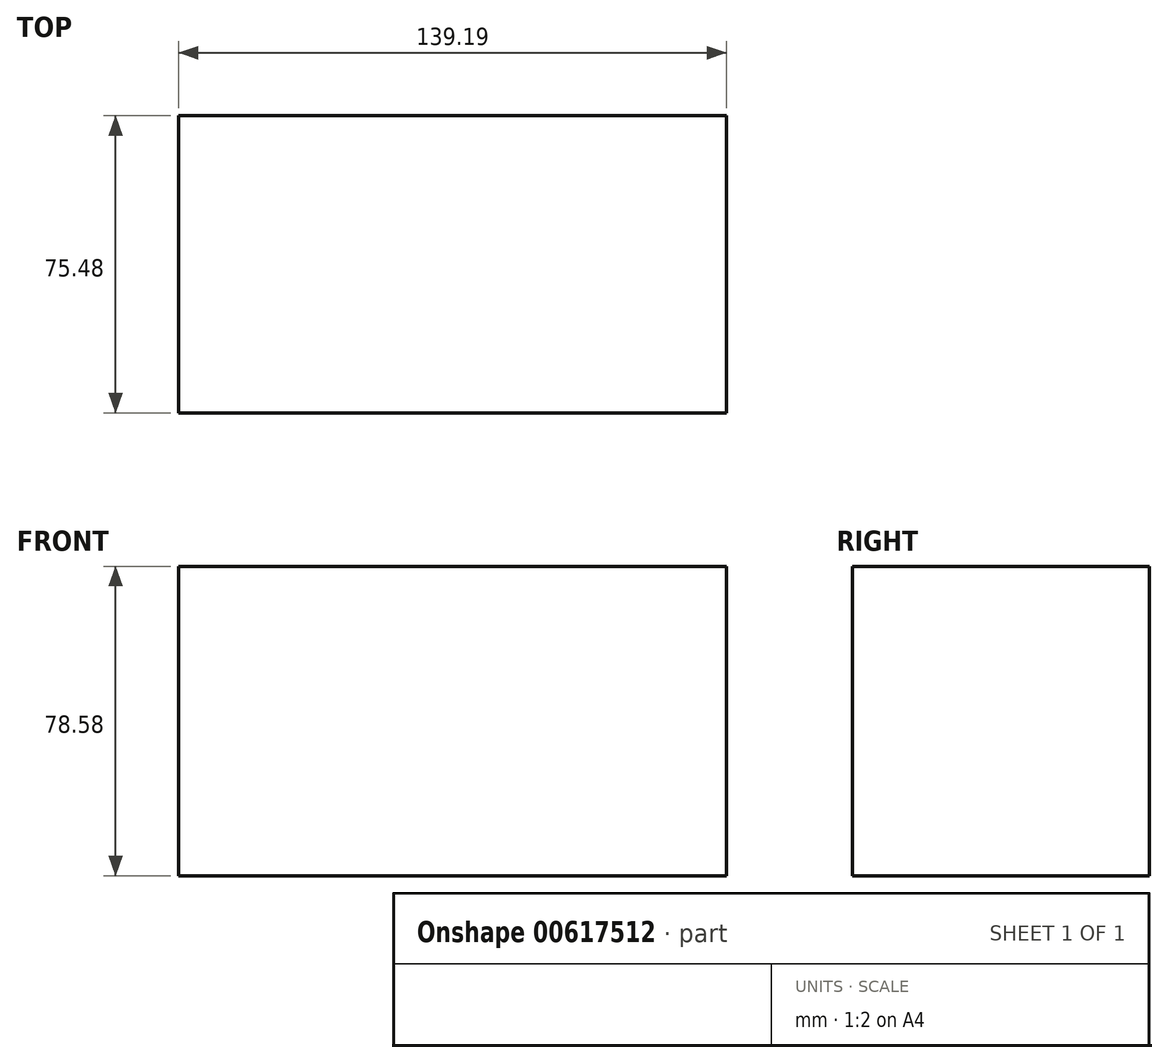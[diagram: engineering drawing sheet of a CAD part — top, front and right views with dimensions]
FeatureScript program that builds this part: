
annotation { "Feature Type Name" : "Feature", "Feature Type Description" : "" }
export const myFeature = defineFeature(function(context is Context, id is Id, definition is map)
    precondition{}
    {
        {
            var Q0;
            Q0=qCreatedBy(makeId("Right.planeOp"),FACE);
            var sketch = newSketch(context, id + "F0", { "sketchPlane" : qUnion([Q0])});
            skLineSegment(sketch, "E0.bottom", {"start": v(-44.54, 56.43) * mm, "end": v(30.94, 56.43) * mm});
            skLineSegment(sketch, "E0.top", {"start": v(-44.54, -22.15) * mm, "end": v(30.94, -22.15) * mm});
            skLineSegment(sketch, "E0.left", {"start": v(-44.54, 56.43) * mm, "end": v(-44.54, -22.15) * mm});
            skLineSegment(sketch, "E0.right", {"start": v(30.94, 56.43) * mm, "end": v(30.94, -22.15) * mm});
            skSolve(sketch);
        }
        {
            var Q0;
            Q0=makeQuery(id+"F0.imprint","IMPRINT",FACE,{"disambiguationData":[TD([[makeQuery(id+"F0.imprint","IMPRINT",EDGE,{"derivedFrom":sQuery(id+"F0.wireOp",EDGE,"E0.bottom")}),-1.0]])]});
            extrude(context, id + "F1", {"entities" : qUnion([Q0]), "depth" : 139.2 * mm, "offsetDistance" : 25.4 * mm});
        }
    });
